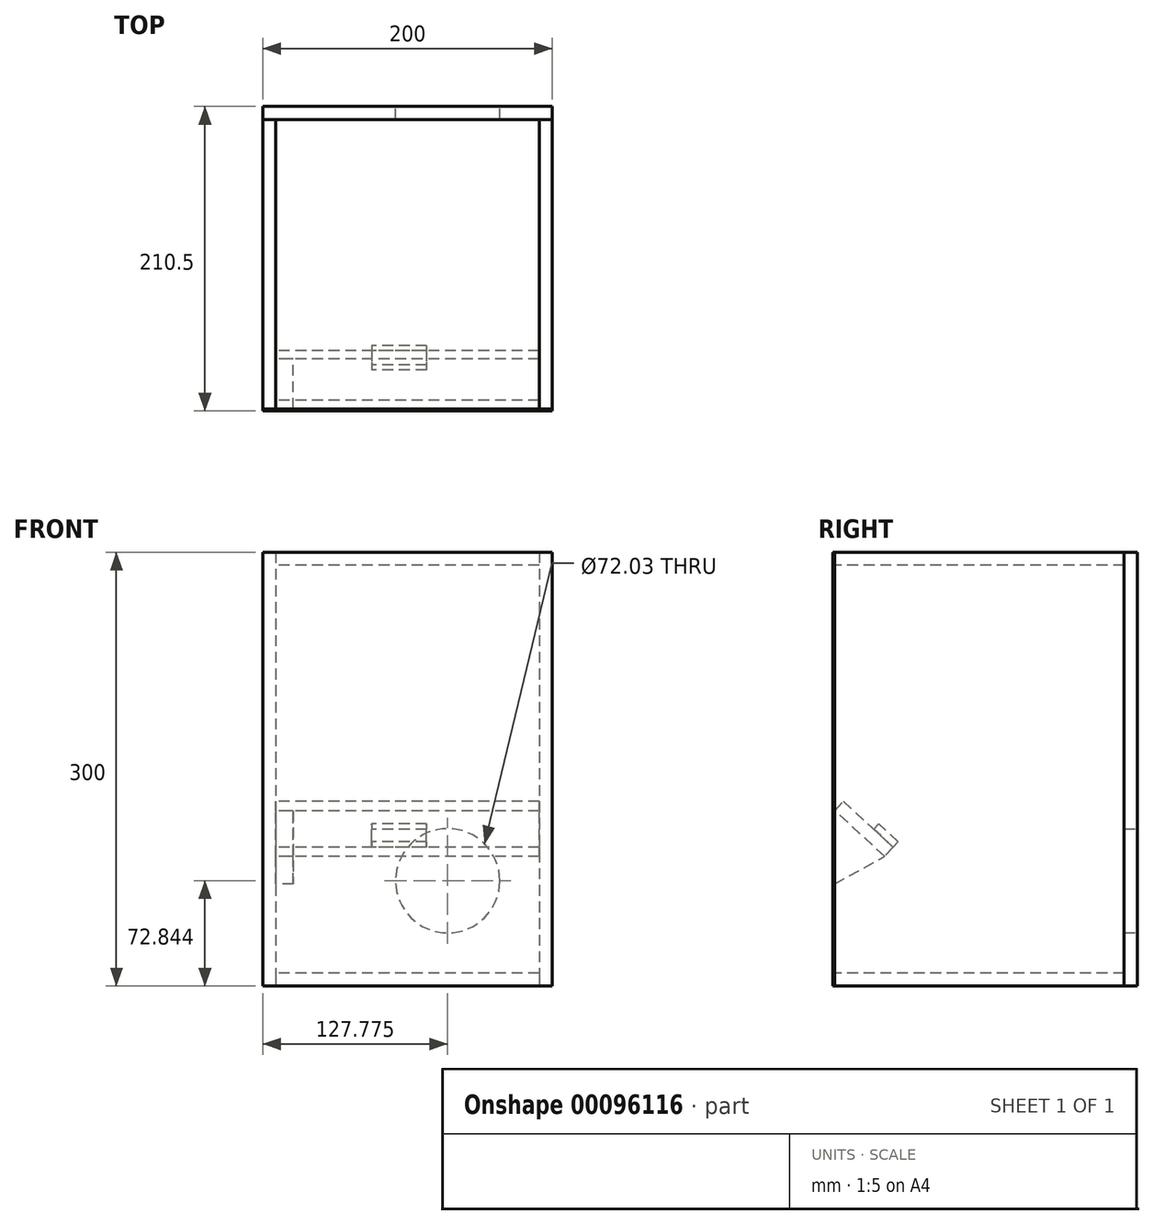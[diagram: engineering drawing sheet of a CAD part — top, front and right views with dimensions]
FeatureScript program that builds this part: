
annotation { "Feature Type Name" : "Feature", "Feature Type Description" : "" }
export const myFeature = defineFeature(function(context is Context, id is Id, definition is map)
    precondition{}
    {
        {
            var Q0;
            Q0=qCreatedBy(makeId("Front.planeOp"),FACE);
            var sketch = newSketch(context, id + "F0", { "sketchPlane" : qUnion([Q0])});
            skLineSegment(sketch, "E0.bottom", {"start": v(0, 0) * mm, "end": v(200, 0) * mm});
            skLineSegment(sketch, "E0.top", {"start": v(0, 300) * mm, "end": v(200, 300) * mm});
            skLineSegment(sketch, "E0.left", {"start": v(0, 0) * mm, "end": v(0, 300) * mm});
            skLineSegment(sketch, "E0.right", {"start": v(200, 0) * mm, "end": v(200, 300) * mm});
            skSolve(sketch);
        }
        {
            var Q0;
            Q0 = qSketchRegion(id + "F0", true);
            extrude(context, id + "F1", {"entities" : qUnion([Q0]), "depth" : 1.5 * mm});
        }
        {
            var Q0;
            Q0=makeQuery(id+"F1.opExtrude","CAP_FACE",FACE,{"disambiguationData":[OSD([sQuery(id+"F0.wireOp",EDGE,"E0.bottom"),sQuery(id+"F0.wireOp",EDGE,"E0.top"),sQuery(id+"F0.wireOp",EDGE,"E0.left"),sQuery(id+"F0.wireOp",EDGE,"E0.right")])],"isStart":true});
            var sketch = newSketch(context, id + "F2", { "sketchPlane" : qUnion([Q0])});
            skLineSegment(sketch, "E1.bottom", {"start": v(0, 300) * mm, "end": v(-9, 300) * mm});
            skLineSegment(sketch, "E1.top", {"start": v(0, 0) * mm, "end": v(-9, 0) * mm});
            skLineSegment(sketch, "E1.left", {"start": v(0, 300) * mm, "end": v(0, 0) * mm});
            skLineSegment(sketch, "E1.right", {"start": v(-9, 300) * mm, "end": v(-9, 0) * mm});
            skSolve(sketch);
        }
        {
            var Q0;
            Q0 = qSketchRegion(id + "F2", true);
            extrude(context, id + "F3", {"entities" : qUnion([Q0]), "depth" : 200 * mm});
        }
        {
            var Q0;
            Q0=makeQuery(id+"F3.opExtrude","SWEPT_FACE",FACE,{"disambiguationData":[OSD([sQuery(id+"F2.wireOp",EDGE,"E1.right")])]});
            var sketch = newSketch(context, id + "F4", { "sketchPlane" : qUnion([Q0])});
            skLineSegment(sketch, "E2", {"start": v(0, 121.24) * mm, "end": v(0, 70.7) * mm});
            skLineSegment(sketch, "E3", {"start": v(0, 70.7) * mm, "end": v(34.4, 89.67) * mm});
            skLineSegment(sketch, "E4", {"start": v(34.4, 89.67) * mm, "end": v(0, 121.24) * mm});
            skSolve(sketch);
        }
        {
            var Q0;
            Q0 = qSketchRegion(id + "F4", true);
            extrude(context, id + "F5", {"entities" : qUnion([Q0]), "depth" : 12 * mm});
        }
        {
            var Q0;
            Q0=makeQuery(id+"F3.opExtrude","SWEPT_FACE",FACE,{"disambiguationData":[OSD([sQuery(id+"F2.wireOp",EDGE,"E1.right")])]});
            var sketch = newSketch(context, id + "F6", { "sketchPlane" : qUnion([Q0])});
            skLineSegment(sketch, "E5", {"start": v(34.4, 89.67) * mm, "end": v(0, 121.24) * mm});
            skLineSegment(sketch, "E6", {"start": v(0, 121.24) * mm, "end": v(5.94, 127.72) * mm});
            skLineSegment(sketch, "E7", {"start": v(5.94, 127.72) * mm, "end": v(40.35, 96.14) * mm});
            skLineSegment(sketch, "E8", {"start": v(40.35, 96.14) * mm, "end": v(34.4, 89.67) * mm});
            skSolve(sketch);
        }
        {
            var Q0;
            Q0 = qSketchRegion(id + "F6", true);
            extrude(context, id + "F7", {"entities" : qUnion([Q0]), "depth" : 182 * mm});
        }
        {
            var Q0;
            Q0=makeQuery(id+"F7.opExtrude","SWEPT_FACE",FACE,{"disambiguationData":[OSD([sQuery(id+"F6.wireOp",EDGE,"E7")])]});
            var sketch = newSketch(context, id + "F8", { "sketchPlane" : qUnion([Q0])});
            skLineSegment(sketch, "E9.bottom", {"start": v(113.07, -35.28) * mm, "end": v(75.26, -35.28) * mm});
            skLineSegment(sketch, "E9.top", {"start": v(113.07, -53.52) * mm, "end": v(75.26, -53.52) * mm});
            skLineSegment(sketch, "E9.left", {"start": v(113.07, -35.28) * mm, "end": v(113.07, -53.52) * mm});
            skLineSegment(sketch, "E9.right", {"start": v(75.26, -35.28) * mm, "end": v(75.26, -53.52) * mm});
            skSolve(sketch);
        }
        {
            var Q0;
            Q0=makeQuery(id+"F8.imprint","IMPRINT",FACE,{"disambiguationData":[TD([[makeQuery(id+"F8.imprint","IMPRINT",EDGE,{"derivedFrom":sQuery(id+"F8.wireOp",EDGE,"E9.bottom")}),1.0]])]});
            extrude(context, id + "F9", {"entities" : qUnion([Q0]), "depth" : 5 * mm});
        }
        {
            var Q0;
            Q0=makeQuery(id+"F3.opExtrude","SWEPT_FACE",FACE,{"disambiguationData":[OSD([sQuery(id+"F2.wireOp",EDGE,"E1.right")])]});
            var sketch = newSketch(context, id + "F10", { "sketchPlane" : qUnion([Q0])});
            skLineSegment(sketch, "E10.bottom", {"start": v(200, 300) * mm, "end": v(0, 300) * mm});
            skLineSegment(sketch, "E10.top", {"start": v(200, 291) * mm, "end": v(0, 291) * mm});
            skLineSegment(sketch, "E10.left", {"start": v(200, 300) * mm, "end": v(200, 291) * mm});
            skLineSegment(sketch, "E10.right", {"start": v(0, 300) * mm, "end": v(0, 291) * mm});
            skSolve(sketch);
        }
        {
            var Q0;
            Q0 = qSketchRegion(id + "F10", true);
            extrude(context, id + "F11", {"entities" : qUnion([Q0]), "depth" : 182 * mm});
        }
        {
            var Q0;
            Q0=makeQuery(id+"F3.opExtrude","SWEPT_FACE",FACE,{"disambiguationData":[OSD([sQuery(id+"F2.wireOp",EDGE,"E1.right")])]});
            var sketch = newSketch(context, id + "F12", { "sketchPlane" : qUnion([Q0])});
            skLineSegment(sketch, "E11.bottom", {"start": v(200, 0) * mm, "end": v(0, 0) * mm});
            skLineSegment(sketch, "E11.top", {"start": v(200, 9) * mm, "end": v(0, 9) * mm});
            skLineSegment(sketch, "E11.left", {"start": v(200, 0) * mm, "end": v(200, 9) * mm});
            skLineSegment(sketch, "E11.right", {"start": v(0, 0) * mm, "end": v(0, 9) * mm});
            skSolve(sketch);
        }
        {
            var Q0;
            Q0 = qSketchRegion(id + "F12", true);
            extrude(context, id + "F13", {"entities" : qUnion([Q0]), "depth" : 182 * mm});
        }
        {
            var Q0;
            Q0=makeQuery(id+"F11.opExtrude","CAP_FACE",FACE,{"disambiguationData":[OSD([sQuery(id+"F10.wireOp",EDGE,"E10.bottom"),sQuery(id+"F10.wireOp",EDGE,"E10.top"),sQuery(id+"F10.wireOp",EDGE,"E10.left"),sQuery(id+"F10.wireOp",EDGE,"E10.right")])],"isStart":false});
            var sketch = newSketch(context, id + "F14", { "sketchPlane" : qUnion([Q0])});
            skLineSegment(sketch, "E12.bottom", {"start": v(200, 300) * mm, "end": v(0, 300) * mm});
            skLineSegment(sketch, "E12.top", {"start": v(200, 0) * mm, "end": v(0, 0) * mm});
            skLineSegment(sketch, "E12.left", {"start": v(200, 300) * mm, "end": v(200, 0) * mm});
            skLineSegment(sketch, "E12.right", {"start": v(0, 300) * mm, "end": v(0, 0) * mm});
            skSolve(sketch);
        }
        {
            var Q0;
            Q0 = qSketchRegion(id + "F14", true);
            extrude(context, id + "F15", {"entities" : qUnion([Q0]), "depth" : 9 * mm});
        }
        {
            var Q0;
            Q0=makeQuery(id+"F15.opExtrude","SWEPT_FACE",FACE,{"disambiguationData":[OSD([sQuery(id+"F14.wireOp",EDGE,"E12.left")])]});
            var sketch = newSketch(context, id + "F16", { "sketchPlane" : qUnion([Q0])});
            skLineSegment(sketch, "E13.bottom", {"start": v(-200, 300) * mm, "end": v(0, 300) * mm});
            skLineSegment(sketch, "E13.top", {"start": v(-200, 0) * mm, "end": v(0, 0) * mm});
            skLineSegment(sketch, "E13.left", {"start": v(-200, 300) * mm, "end": v(-200, 0) * mm});
            skLineSegment(sketch, "E13.right", {"start": v(0, 300) * mm, "end": v(0, 0) * mm});
            skSolve(sketch);
        }
        {
            var Q0;
            Q0 = qSketchRegion(id + "F16", true);
            extrude(context, id + "F17", {"entities" : qUnion([Q0]), "depth" : 9 * mm});
        }
        {
            var Q0;
            Q0=makeQuery(id+"F17.opExtrude","CAP_FACE",FACE,{"disambiguationData":[OSD([sQuery(id+"F16.wireOp",EDGE,"E13.bottom"),sQuery(id+"F16.wireOp",EDGE,"E13.top"),sQuery(id+"F16.wireOp",EDGE,"E13.left"),sQuery(id+"F16.wireOp",EDGE,"E13.right")])],"isStart":false});
            var sketch = newSketch(context, id + "F18", { "sketchPlane" : qUnion([Q0])});
            skCircle(sketch, "E14", {"center": v(-127.78, 72.84) * mm, "radius": 36.02 * mm});
            skSolve(sketch);
        }
        {
            var Q0;
            Q0 = qSketchRegion(id + "F18", true);
            extrude(context, id + "F19", {"entities" : qUnion([Q0]), "operationType" : NewBodyOperationType.REMOVE, "oppositeDirection" : true, "depth" : 9 * mm});
        }
    });
